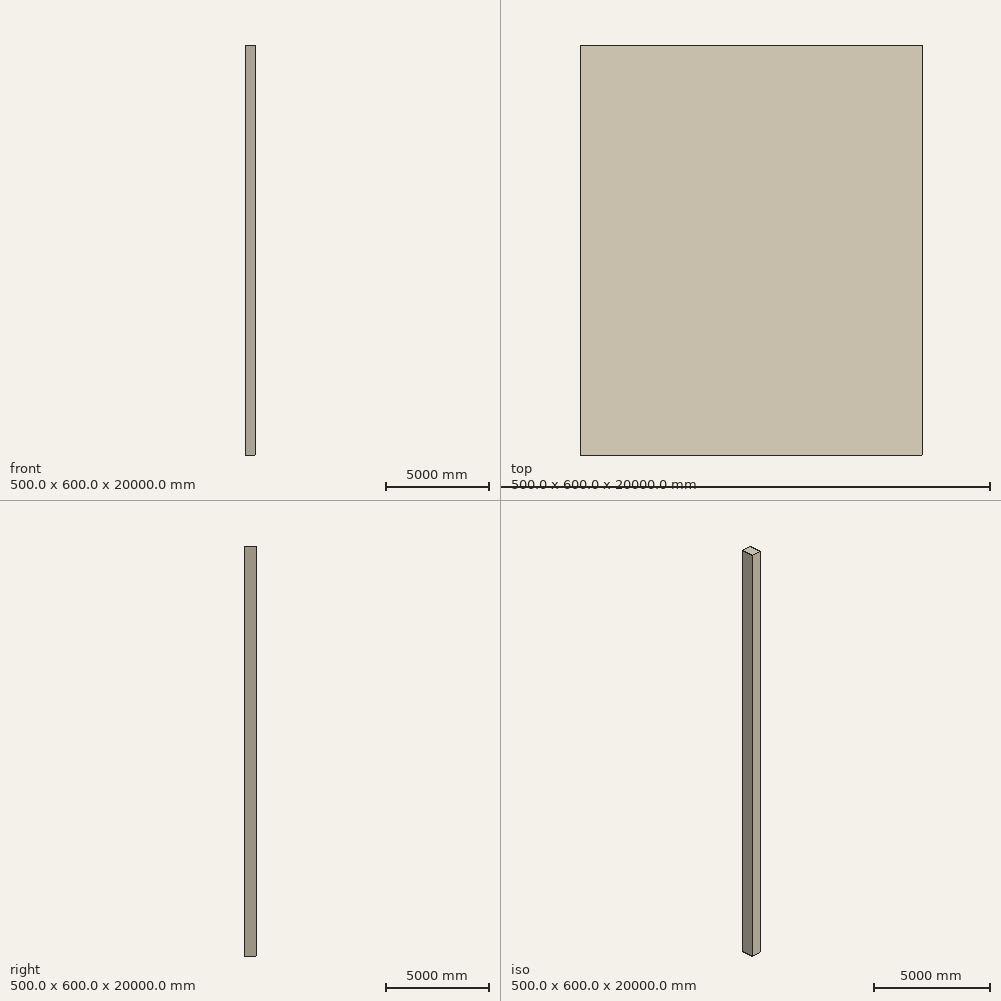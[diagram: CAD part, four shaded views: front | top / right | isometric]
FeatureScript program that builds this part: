
annotation { "Feature Type Name" : "Feature", "Feature Type Description" : "" }
export const myFeature = defineFeature(function(context is Context, id is Id, definition is map)
    precondition{}
    {
        {
            var Q0;
            Q0=qCreatedBy(makeId("Top.planeOp"),FACE);
            var sketch = newSketch(context, id + "F0", { "sketchPlane" : qUnion([Q0])});
            skLineSegment(sketch, "E0.bottom", {"start": v(0, 0) * mm, "end": v(500, 0) * mm});
            skLineSegment(sketch, "E0.top", {"start": v(0, 600) * mm, "end": v(500, 600) * mm});
            skLineSegment(sketch, "E0.left", {"start": v(0, 0) * mm, "end": v(0, 600) * mm});
            skLineSegment(sketch, "E0.right", {"start": v(500, 0) * mm, "end": v(500, 600) * mm});
            skSolve(sketch);
        }
        {
            assignVariable(context, id + "F1", {"variableType" : VariableType.LENGTH, "name" : "hauteur", "lengthValue" : 20000 * mm});
        }
        {
            var Q0;
            Q0 = qSketchRegion(id + "F0", true);
            extrude(context, id + "F2", {"entities" : qUnion([Q0]), "oppositeDirection" : true, "depth" : getVariable(context, 'hauteur'), "offsetDistance" : 25 * mm});
        }
    });
